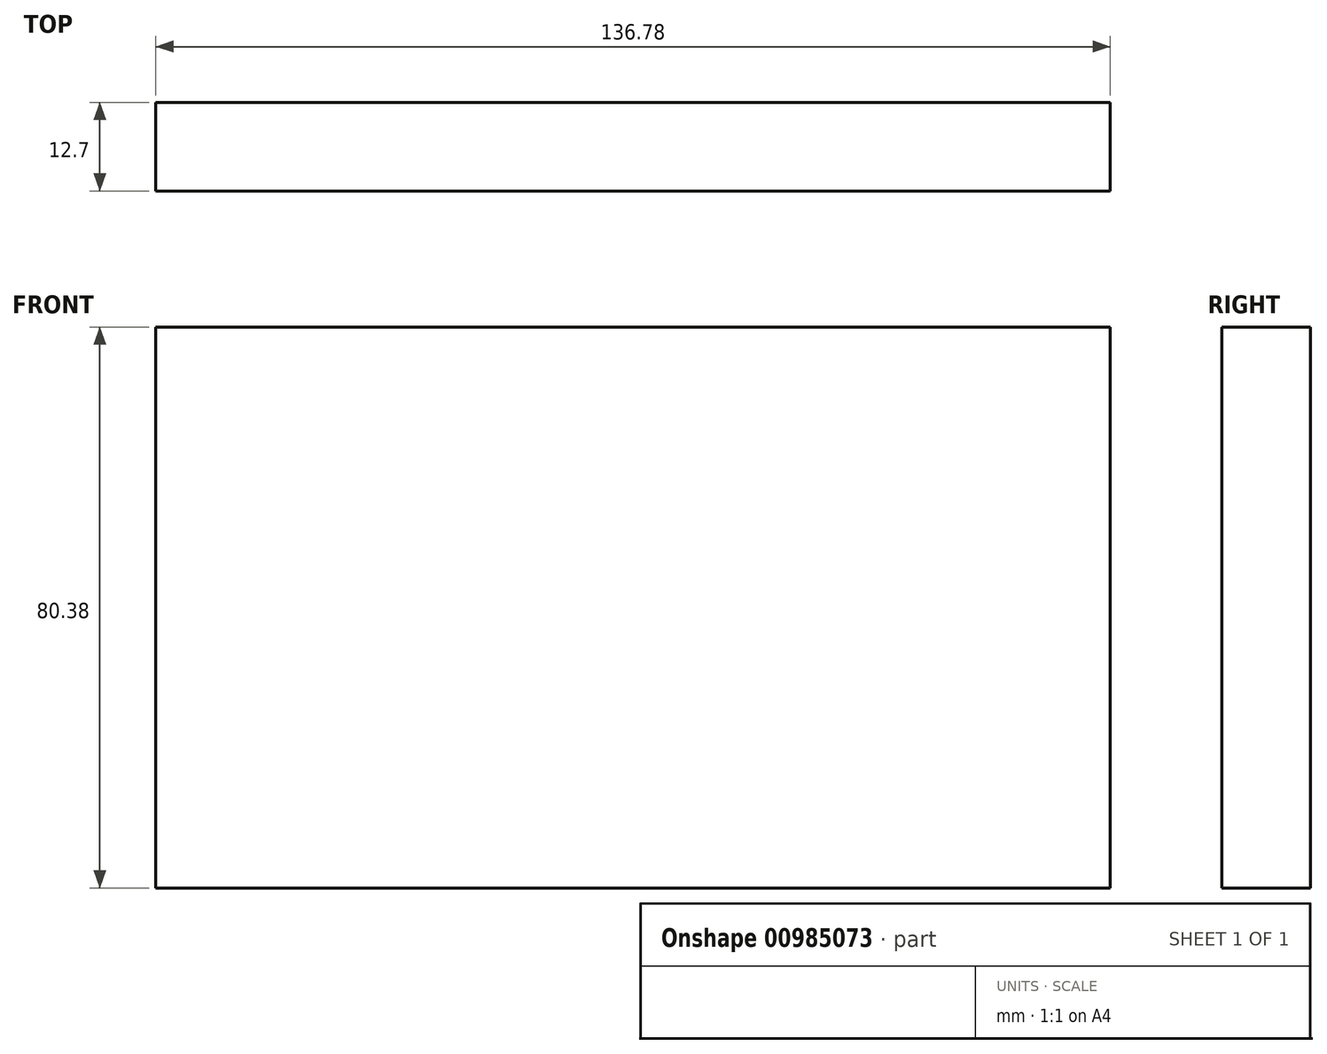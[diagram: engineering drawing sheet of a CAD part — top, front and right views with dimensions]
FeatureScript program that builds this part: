
annotation { "Feature Type Name" : "Feature", "Feature Type Description" : "" }
export const myFeature = defineFeature(function(context is Context, id is Id, definition is map)
    precondition{}
    {
        {
            var Q0;
            Q0=qCreatedBy(makeId("Front.planeOp"),FACE);
            var sketch = newSketch(context, id + "F0", { "sketchPlane" : qUnion([Q0])});
            skLineSegment(sketch, "E0.bottom", {"start": v(18.64, 0) * mm, "end": v(-118.14, 0) * mm});
            skLineSegment(sketch, "E0.top", {"start": v(18.64, 80.38) * mm, "end": v(-118.14, 80.38) * mm});
            skLineSegment(sketch, "E0.left", {"start": v(18.64, 0) * mm, "end": v(18.64, 80.38) * mm});
            skLineSegment(sketch, "E0.right", {"start": v(-118.14, 0) * mm, "end": v(-118.14, 80.38) * mm});
            skPoint(sketch, "E0.middle", {"position": v(-49.75, 40.2) * mm});
            skSolve(sketch);
        }
        {
            var Q0;
            Q0=makeQuery(id+"F0.imprint","IMPRINT",FACE,{"disambiguationData":[TD([[makeQuery(id+"F0.imprint","IMPRINT",EDGE,{"derivedFrom":sQuery(id+"F0.wireOp",EDGE,"E0.bottom")}),-1.0]])]});
            extrude(context, id + "F1", {"entities" : qUnion([Q0]), "depth" : 12.7 * mm, "offsetDistance" : 25.4 * mm});
        }
    });
